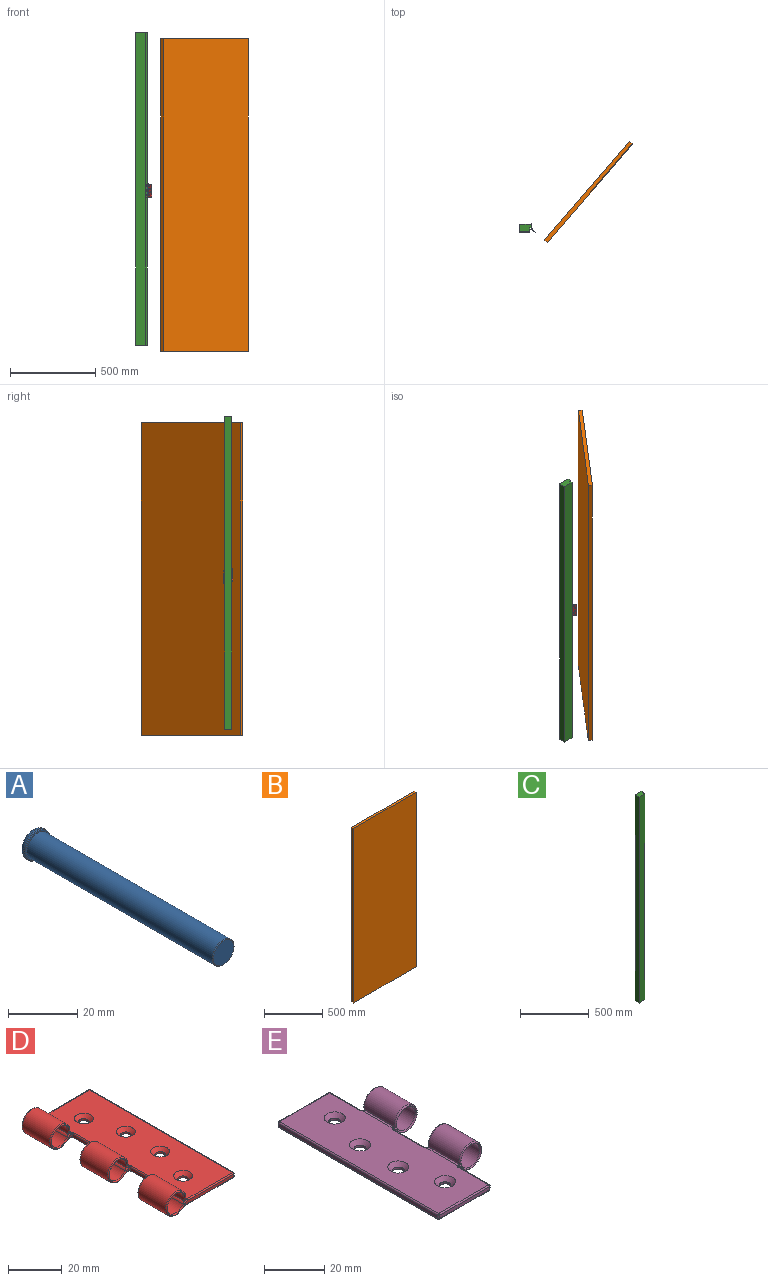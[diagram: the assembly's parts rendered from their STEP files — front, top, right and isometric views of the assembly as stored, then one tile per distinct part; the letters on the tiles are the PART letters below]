
ASSEMBLY  parts=5 mates=5
PART A: 8 faces, bbox 11x78.2x11 mm
  f0: cylinder r=4.4mm len=75.8mm, axis (0,1,0), area 2095.6mm2, adj f2,f5
  f1: plane 8.4x8.4mm, normal (0,-1,0), area 55.4mm2, adj f2
  f2: torus R=4.2mm, axis (0,-1,0), area 8.5mm2, adj f0,f1
  f3: cylinder r=5.1mm len=10.21mm, axis (0,-1,0), area 16mm2, adj f6,f7
  f4: plane 7.21x7.21mm, normal (0,1,0), area 40.8mm2, adj f6
  f5: plane 9.81x9.81mm, normal (0,-1,0), area 14.7mm2, adj f0,f7
  f6: torus R=3.6mm, axis (0,1,0), area 67.5mm2, adj f3,f4
  f7: torus R=4.9mm, axis (0,1,0), area 9.9mm2, adj f3,f5
PART B: 6 faces, bbox 762x23x1828.8 mm
  f0: plane 1828.8x23mm, normal (-1,0,0), area 42062.4mm2, adj f1,f3,f4,f5
  f1: plane 1828.8x762mm, normal (0,-1,0), area 1393545.6mm2, adj f0,f2,f4,f5
  f2: plane 1828.8x23mm, normal (1,0,0), area 42062.4mm2, adj f1,f3,f4,f5
  f3: plane 1828.8x762mm, normal (0,1,0), area 1393545.6mm2, adj f0,f2,f4,f5
  f4: plane 762x23mm, normal (0,0,1), area 17526mm2, adj f0,f1,f2,f3
  f5: plane 762x23mm, normal (0,0,-1), area 17526mm2, adj f0,f1,f2,f3
PART C: 8 faces, bbox 68.4x42x1828.8 mm
  f0: plane 1828.8x21mm, normal (1,0,0), area 38404.8mm2, adj f1,f5,f6,f7
  f1: plane 1828.8x8mm, normal (0,-1,0), area 14630.4mm2, adj f0,f2,f6,f7
  f2: plane 1828.8x21mm, normal (1,0,0), area 38404.8mm2, adj f1,f3,f6,f7
  f3: plane 1828.8x68.4mm, normal (0,1,0), area 125094mm2, adj f2,f4,f6,f7
  f4: plane 1828.8x42mm, normal (-1,0,0), area 76809.6mm2, adj f3,f5,f6,f7
  f5: plane 1828.8x60.4mm, normal (0,-1,0), area 110463.6mm2, adj f0,f4,f6,f7
  f6: plane 68.4x42mm, normal (0,0,1), area 2704.9mm2, adj f0,f1,f2,f3,f4,f5
  f7: plane 68.4x42mm, normal (0,0,-1), area 2704.9mm2, adj f0,f1,f2,f3,f4,f5
PART D: 94 faces, bbox 36.3x76x11.6 mm
  f0: cylinder r=5.25mm len=14.2mm, axis (0,1,0), area 412.4mm2, adj f2,f8,f69,f87
  f1: cylinder r=5.25mm len=14.2mm, axis (0,1,0), area 412.4mm2, adj f3,f9,f46,f78
  f2: plane 15.21x0.8mm, normal (0,0,-1), area 11.4mm2, adj f0,f4,f69,f71,f87,f90
  f3: plane 15.21x0.8mm, normal (0,0,-1), area 11.4mm2, adj f1,f5,f45,f46,f78,f80
  f4: cylinder r=4.5mm len=14.2mm, axis (0,1,0), area 382.9mm2, adj f2,f6,f71,f90
  f5: cylinder r=4.5mm len=14.2mm, axis (0,1,0), area 382.9mm2, adj f3,f7,f45,f80
  f6: cylinder r=2.39mm len=14.47mm, axis (0,1,0), area 36mm2, adj f4,f14,f73,f75,f92,f93
  f7: cylinder r=2.39mm len=14.33mm, axis (0,1,0), area 35.9mm2, adj f5,f14,f43,f82,f84
  f8: cylinder r=4.96mm len=14.47mm, axis (0,1,0), area 44.3mm2, adj f0,f16,f66,f68,f85,f88
  f9: cylinder r=4.96mm len=14.33mm, axis (0,1,0), area 44.3mm2, adj f1,f16,f48,f76,f77
  f10: cylinder r=5.25mm len=14.2mm, axis (0,1,0), area 412.4mm2, adj f11,f17,f51,f60
  f11: plane 15.21x0.8mm, normal (0,0,-1), area 11.4mm2, adj f10,f12,f51,f52,f60,f63
  f12: cylinder r=4.5mm len=14.2mm, axis (0,1,0), area 382.9mm2, adj f11,f13,f52,f63
  f13: cylinder r=2.39mm len=14.33mm, axis (0,1,0), area 35.9mm2, adj f12,f14,f49,f65,f67
  f14: plane 75x24mm, normal (0,0,1), area 1630.6mm2, adj f6,f7,f13,f21,f23,f25,f27,f41
  f15: plane 75x1.3mm, normal (1,0,0), area 97.5mm2, adj f38,f39,f42,f55
  f16: plane 75x24mm, normal (0,0,-1), area 1734.3mm2, adj f8,f9,f17,f20,f22,f24,f26,f50
  f17: cylinder r=4.96mm len=14.33mm, axis (0,1,0), area 44.3mm2, adj f10,f16,f54,f58,f61
  f18: plane 26.22x1.77mm, normal (0,-1,0), area 33.2mm2, adj f39,f47,f49,f52,f54,f56
  f19: plane 26.22x1.77mm, normal (0,1,0), area 33.2mm2, adj f38,f41,f43,f45,f48,f50
  f20: cylinder r=2mm len=4mm, axis (0,0,1), area 10.1mm2, adj f16,f21
  f21: cone r=2mm half-angle=45deg, axis (0,0,1), area 36.7mm2, adj f14,f20
  f22: cylinder r=2mm len=4mm, axis (0,0,1), area 10.1mm2, adj f16,f23
  f23: cone r=2mm half-angle=45deg, axis (0,0,1), area 36.7mm2, adj f14,f22
  f24: cylinder r=2mm len=4mm, axis (0,0,1), area 10.1mm2, adj f16,f25
  f25: cone r=2mm half-angle=45deg, axis (0,0,1), area 36.7mm2, adj f14,f24
  f26: cylinder r=2mm len=4mm, axis (0,0,1), area 10.1mm2, adj f16,f27
  f27: cone r=2mm half-angle=45deg, axis (0,0,1), area 36.7mm2, adj f14,f26
  f28: plane 14.2x1.3mm, normal (-1,0,0), area 18.5mm2, adj f34,f35,f81,f89
  f29: plane 1.72x1.7mm, normal (0,-1,0), area 1.3mm2, adj f34,f77,f80,f82
  f30: plane 1.72x1.7mm, normal (0,1,0), area 1.3mm2, adj f35,f88,f90,f92
  f31: plane 14.2x1.3mm, normal (-1,0,0), area 18.5mm2, adj f36,f37,f62,f72
  f32: plane 1.72x1.7mm, normal (0,1,0), area 1.3mm2, adj f36,f61,f63,f65
  f33: plane 1.72x1.7mm, normal (0,-1,0), area 1.3mm2, adj f37,f68,f71,f73
  f34: cylinder r=0.5mm len=1.32mm, axis (0,0,-1), area 1mm2, adj f28,f29,f76,f79,f84,f86
  f35: cylinder r=0.5mm len=1.32mm, axis (0,0,1), area 1mm2, adj f28,f30,f83,f85,f91,f93
  f36: cylinder r=0.5mm len=1.32mm, axis (0,0,-1), area 1mm2, adj f31,f32,f58,f59,f67,f70
  f37: cylinder r=0.5mm len=1.32mm, axis (0,0,1), area 1mm2, adj f31,f33,f64,f66,f74,f75
  f38: cylinder r=0.5mm len=1.3mm, axis (0,0,-1), area 1mm2, adj f15,f19,f40,f53
  f39: cylinder r=0.5mm len=1.3mm, axis (0,0,1), area 1mm2, adj f15,f18,f44,f57
  f40: sphere r=0.5mm, area 0.4mm2, adj f38,f41,f42
  f41: cylinder r=0.5mm len=24mm, axis (1,0,0), area 18.8mm2, adj f14,f19,f40,f43
  f42: cylinder r=0.5mm len=75mm, axis (0,1,0), area 58.9mm2, adj f14,f15,f40,f44
  f43: torus R=1.89mm, axis (0,-1,0), area 1.8mm2, adj f7,f19,f41,f45
  f44: sphere r=0.5mm, area 0.4mm2, adj f39,f42,f47
  f45: torus R=5mm, axis (0,-1,0), area 18.5mm2, adj f3,f5,f19,f43,f46,f48
  f46: torus R=4.75mm, axis (0,-1,0), area 18.7mm2, adj f1,f3,f45,f48
  f47: cylinder r=0.5mm len=24mm, axis (-1,0,0), area 18.8mm2, adj f14,f18,f44,f49
  f48: torus R=5.46mm, axis (0,-1,0), area 2.5mm2, adj f9,f19,f45,f46,f50
  f49: torus R=1.89mm, axis (0,-1,0), area 1.8mm2, adj f13,f18,f47,f52
  f50: cylinder r=0.5mm len=24mm, axis (-1,0,0), area 18.8mm2, adj f16,f19,f48,f53
  f51: torus R=4.75mm, axis (0,-1,0), area 18.7mm2, adj f10,f11,f52,f54
  f52: torus R=5mm, axis (0,-1,0), area 18.5mm2, adj f11,f12,f18,f49,f51,f54
  f53: sphere r=0.5mm, area 0.4mm2, adj f38,f50,f55
  f54: torus R=5.46mm, axis (0,-1,0), area 2.5mm2, adj f17,f18,f51,f52,f56
  f55: cylinder r=0.5mm len=75mm, axis (0,1,0), area 58.9mm2, adj f15,f16,f53,f57
  f56: cylinder r=0.5mm len=24mm, axis (1,0,0), area 18.8mm2, adj f16,f18,f54,f57
  f57: sphere r=0.5mm, area 0.4mm2, adj f39,f55,f56
  f58: bspline ~0.72x0.61mm, area 0.3mm2, adj f17,f36,f59,f61
  f59: torus R=1mm, axis (0,0,1), area 0.6mm2, adj f16,f36,f58,f62
  f60: torus R=4.75mm, axis (0,-1,0), area 18.7mm2, adj f10,f11,f61,f63
  f61: torus R=5.46mm, axis (0,-1,0), area 2.1mm2, adj f17,f32,f58,f60,f63
  f62: cylinder r=0.5mm len=14.2mm, axis (0,-1,0), area 11.2mm2, adj f16,f31,f59,f64
  f63: torus R=5mm, axis (0,-1,0), area 18.5mm2, adj f11,f12,f32,f60,f61,f65
  f64: torus R=1mm, axis (0,0,1), area 0.6mm2, adj f16,f37,f62,f66
  f65: torus R=1.89mm, axis (0,-1,0), area 1.4mm2, adj f13,f32,f63,f67
  f66: bspline ~0.72x0.61mm, area 0.3mm2, adj f8,f37,f64,f68
  f67: bspline ~0.83x0.6mm, area 0.3mm2, adj f13,f36,f65,f70
  f68: torus R=5.46mm, axis (0,-1,0), area 2.1mm2, adj f8,f33,f66,f69,f71
  f69: torus R=4.75mm, axis (0,-1,0), area 18.7mm2, adj f0,f2,f68,f71
  f70: torus R=1mm, axis (0,0,-1), area 0.6mm2, adj f14,f36,f67,f72
  f71: torus R=5mm, axis (0,-1,0), area 18.5mm2, adj f2,f4,f33,f68,f69,f73
  f72: cylinder r=0.5mm len=14.2mm, axis (0,-1,0), area 11.2mm2, adj f14,f31,f70,f74
  f73: torus R=1.89mm, axis (0,-1,0), area 1.4mm2, adj f6,f33,f71,f75
  f74: torus R=1mm, axis (0,0,-1), area 0.6mm2, adj f14,f37,f72,f75
  f75: bspline ~0.83x0.6mm, area 0.3mm2, adj f6,f37,f73,f74
  f76: bspline ~0.72x0.61mm, area 0.3mm2, adj f9,f34,f77,f79
  f77: torus R=5.46mm, axis (0,-1,0), area 2.1mm2, adj f9,f29,f76,f78,f80
  f78: torus R=4.75mm, axis (0,-1,0), area 18.7mm2, adj f1,f3,f77,f80
  f79: torus R=1mm, axis (0,0,1), area 0.6mm2, adj f16,f34,f76,f81
  f80: torus R=5mm, axis (0,-1,0), area 18.5mm2, adj f3,f5,f29,f77,f78,f82
  f81: cylinder r=0.5mm len=14.2mm, axis (0,1,0), area 11.2mm2, adj f16,f28,f79,f83
  f82: torus R=1.89mm, axis (0,-1,0), area 1.4mm2, adj f7,f29,f80,f84
  f83: torus R=1mm, axis (0,0,1), area 0.6mm2, adj f16,f35,f81,f85
  f84: bspline ~0.83x0.6mm, area 0.3mm2, adj f7,f34,f82,f86
  f85: bspline ~0.72x0.61mm, area 0.3mm2, adj f8,f35,f83,f88
  f86: torus R=1mm, axis (0,0,-1), area 0.6mm2, adj f14,f34,f84,f89
  f87: torus R=4.75mm, axis (0,-1,0), area 18.7mm2, adj f0,f2,f88,f90
  f88: torus R=5.46mm, axis (0,-1,0), area 2.1mm2, adj f8,f30,f85,f87,f90
  f89: cylinder r=0.5mm len=14.2mm, axis (0,-1,0), area 11.2mm2, adj f14,f28,f86,f91
  f90: torus R=5mm, axis (0,-1,0), area 18.5mm2, adj f2,f4,f30,f87,f88,f92
  f91: torus R=1mm, axis (0,0,-1), area 0.6mm2, adj f14,f35,f89,f93
  f92: torus R=1.89mm, axis (0,-1,0), area 1.4mm2, adj f6,f30,f90,f93
  f93: bspline ~0.83x0.6mm, area 0.3mm2, adj f6,f35,f91,f92
PART E: 90 faces, bbox 36.3x76x11.6 mm
  f0: cylinder r=5.25mm len=14.2mm, axis (0,1,0), area 412.4mm2, adj f2,f8,f59,f83
  f1: cylinder r=5.25mm len=14.2mm, axis (0,1,0), area 412.4mm2, adj f3,f9,f46,f74
  f2: plane 15.21x0.8mm, normal (0,0,-1), area 11.4mm2, adj f0,f4,f59,f61,f83,f86
  f3: plane 15.21x0.8mm, normal (0,0,-1), area 11.4mm2, adj f1,f5,f46,f49,f74,f76
  f4: cylinder r=4.5mm len=14.2mm, axis (0,1,0), area 382.9mm2, adj f2,f6,f61,f86
  f5: cylinder r=4.5mm len=14.2mm, axis (0,1,0), area 382.9mm2, adj f3,f7,f49,f76
  f6: cylinder r=2.39mm len=14.47mm, axis (0,1,0), area 36mm2, adj f4,f10,f63,f65,f88,f89
  f7: cylinder r=2.39mm len=14.47mm, axis (0,1,0), area 36mm2, adj f5,f10,f51,f53,f78,f80
  f8: cylinder r=4.96mm len=14.47mm, axis (0,1,0), area 44.3mm2, adj f0,f12,f56,f58,f81,f84
  f9: cylinder r=4.96mm len=14.47mm, axis (0,1,0), area 44.3mm2, adj f1,f12,f44,f47,f72,f73
  f10: plane 75x24mm, normal (0,0,1), area 1623.5mm2, adj f6,f7,f16,f18,f20,f22,f55,f57
  f11: plane 75x1.3mm, normal (-1,0,0), area 97.5mm2, adj f36,f37,f43,f66
  f12: plane 75x24mm, normal (0,0,-1), area 1727.2mm2, adj f8,f9,f15,f17,f19,f21,f39,f40
  f13: plane 23.5x1.3mm, normal (0,-1,0), area 30.6mm2, adj f30,f37,f39,f62
  f14: plane 23.5x1.3mm, normal (0,1,0), area 30.6mm2, adj f34,f36,f48,f70
  f15: cylinder r=2mm len=4mm, axis (0,0,1), area 10.1mm2, adj f12,f16
  f16: cone r=2mm half-angle=45deg, axis (0,0,1), area 36.7mm2, adj f10,f15
  f17: cylinder r=2mm len=4mm, axis (0,0,1), area 10.1mm2, adj f12,f18
  f18: cone r=2mm half-angle=45deg, axis (0,0,1), area 36.7mm2, adj f10,f17
  f19: cylinder r=2mm len=4mm, axis (0,0,1), area 10.1mm2, adj f12,f20
  f20: cone r=2mm half-angle=45deg, axis (0,0,1), area 36.7mm2, adj f10,f19
  f21: cylinder r=2mm len=4mm, axis (0,0,1), area 10.1mm2, adj f12,f22
  f22: cone r=2mm half-angle=45deg, axis (0,0,1), area 36.7mm2, adj f10,f21
  f23: plane 14.2x1.3mm, normal (1,0,0), area 18.5mm2, adj f30,f31,f40,f57
  f24: plane 1.72x1.7mm, normal (0,-1,0), area 1.3mm2, adj f31,f47,f49,f51
  f25: plane 14.2x1.3mm, normal (1,0,0), area 18.5mm2, adj f32,f33,f77,f85
  f26: plane 1.72x1.7mm, normal (0,1,0), area 1.3mm2, adj f32,f73,f76,f78
  f27: plane 1.72x1.7mm, normal (0,-1,0), area 1.3mm2, adj f33,f84,f86,f88
  f28: plane 14.2x1.3mm, normal (1,0,0), area 18.5mm2, adj f34,f35,f52,f69
  f29: plane 1.72x1.7mm, normal (0,1,0), area 1.3mm2, adj f35,f58,f61,f63
  f30: cylinder r=0.5mm len=1.3mm, axis (0,0,1), area 1mm2, adj f13,f23,f38,f60
  f31: cylinder r=0.5mm len=1.32mm, axis (0,0,1), area 1mm2, adj f23,f24,f42,f44,f53,f55
  f32: cylinder r=0.5mm len=1.32mm, axis (0,0,-1), area 1mm2, adj f25,f26,f72,f75,f80,f82
  f33: cylinder r=0.5mm len=1.32mm, axis (0,0,1), area 1mm2, adj f25,f27,f79,f81,f87,f89
  f34: cylinder r=0.5mm len=1.3mm, axis (0,0,-1), area 1mm2, adj f14,f28,f50,f71
  f35: cylinder r=0.5mm len=1.32mm, axis (0,0,-1), area 1mm2, adj f28,f29,f54,f56,f65,f67
  f36: cylinder r=0.5mm len=1.3mm, axis (0,0,-1), area 1mm2, adj f11,f14,f45,f68
  f37: cylinder r=0.5mm len=1.3mm, axis (0,0,1), area 1mm2, adj f11,f13,f41,f64
  f38: sphere r=0.5mm, area 0.4mm2, adj f30,f39,f40
  f39: cylinder r=0.5mm len=23.5mm, axis (-1,0,0), area 18.5mm2, adj f12,f13,f38,f41
  f40: cylinder r=0.5mm len=14.2mm, axis (0,1,0), area 11.2mm2, adj f12,f23,f38,f42
  f41: sphere r=0.5mm, area 0.4mm2, adj f37,f39,f43
  f42: torus R=1mm, axis (0,0,1), area 0.6mm2, adj f12,f31,f40,f44
  f43: cylinder r=0.5mm len=75mm, axis (0,1,0), area 58.9mm2, adj f11,f12,f41,f45
  f44: bspline ~0.72x0.61mm, area 0.3mm2, adj f9,f31,f42,f47
  f45: sphere r=0.5mm, area 0.4mm2, adj f36,f43,f48
  f46: torus R=4.75mm, axis (0,1,0), area 18.7mm2, adj f1,f3,f47,f49
  f47: torus R=5.46mm, axis (0,1,0), area 2.1mm2, adj f9,f24,f44,f46,f49
  f48: cylinder r=0.5mm len=23.5mm, axis (1,0,0), area 18.5mm2, adj f12,f14,f45,f50
  f49: torus R=5mm, axis (0,1,0), area 18.5mm2, adj f3,f5,f24,f46,f47,f51
  f50: sphere r=0.5mm, area 0.4mm2, adj f34,f48,f52
  f51: torus R=1.89mm, axis (0,1,0), area 1.4mm2, adj f7,f24,f49,f53
  f52: cylinder r=0.5mm len=14.2mm, axis (0,-1,0), area 11.2mm2, adj f12,f28,f50,f54
  f53: bspline ~0.83x0.6mm, area 0.3mm2, adj f7,f31,f51,f55
  f54: torus R=1mm, axis (0,0,1), area 0.6mm2, adj f12,f35,f52,f56
  f55: torus R=1mm, axis (0,0,-1), area 0.6mm2, adj f10,f31,f53,f57
  f56: bspline ~0.72x0.61mm, area 0.3mm2, adj f8,f35,f54,f58
  f57: cylinder r=0.5mm len=14.2mm, axis (0,1,0), area 11.2mm2, adj f10,f23,f55,f60
  f58: torus R=5.46mm, axis (0,1,0), area 2.1mm2, adj f8,f29,f56,f59,f61
  f59: torus R=4.75mm, axis (0,1,0), area 18.7mm2, adj f0,f2,f58,f61
  f60: sphere r=0.5mm, area 0.4mm2, adj f30,f57,f62
  f61: torus R=5mm, axis (0,1,0), area 18.5mm2, adj f2,f4,f29,f58,f59,f63
  f62: cylinder r=0.5mm len=23.5mm, axis (1,0,0), area 18.5mm2, adj f10,f13,f60,f64
  f63: torus R=1.89mm, axis (0,1,0), area 1.4mm2, adj f6,f29,f61,f65
  f64: sphere r=0.5mm, area 0.4mm2, adj f37,f62,f66
  f65: bspline ~0.83x0.6mm, area 0.3mm2, adj f6,f35,f63,f67
  f66: cylinder r=0.5mm len=75mm, axis (0,1,0), area 58.9mm2, adj f10,f11,f64,f68
  f67: torus R=1mm, axis (0,0,-1), area 0.6mm2, adj f10,f35,f65,f69
  f68: sphere r=0.5mm, area 0.4mm2, adj f36,f66,f70
  f69: cylinder r=0.5mm len=14.2mm, axis (0,1,0), area 11.2mm2, adj f10,f28,f67,f71
  f70: cylinder r=0.5mm len=23.5mm, axis (-1,0,0), area 18.5mm2, adj f10,f14,f68,f71
  f71: sphere r=0.5mm, area 0.4mm2, adj f34,f69,f70
  f72: bspline ~0.72x0.61mm, area 0.3mm2, adj f9,f32,f73,f75
  f73: torus R=5.46mm, axis (0,1,0), area 2.1mm2, adj f9,f26,f72,f74,f76
  f74: torus R=4.75mm, axis (0,1,0), area 18.7mm2, adj f1,f3,f73,f76
  f75: torus R=1mm, axis (0,0,1), area 0.6mm2, adj f12,f32,f72,f77
  f76: torus R=5mm, axis (0,1,0), area 18.5mm2, adj f3,f5,f26,f73,f74,f78
  f77: cylinder r=0.5mm len=14.2mm, axis (0,1,0), area 11.2mm2, adj f12,f25,f75,f79
  f78: torus R=1.89mm, axis (0,1,0), area 1.4mm2, adj f7,f26,f76,f80
  f79: torus R=1mm, axis (0,0,1), area 0.6mm2, adj f12,f33,f77,f81
  f80: bspline ~0.83x0.6mm, area 0.3mm2, adj f7,f32,f78,f82
  f81: bspline ~0.72x0.61mm, area 0.3mm2, adj f8,f33,f79,f84
  f82: torus R=1mm, axis (0,0,-1), area 0.6mm2, adj f10,f32,f80,f85
  f83: torus R=4.75mm, axis (0,1,0), area 18.7mm2, adj f0,f2,f84,f86
  f84: torus R=5.46mm, axis (0,1,0), area 2.1mm2, adj f8,f27,f81,f83,f86
  f85: cylinder r=0.5mm len=14.2mm, axis (0,1,0), area 11.2mm2, adj f10,f25,f82,f87
  f86: torus R=5mm, axis (0,1,0), area 18.5mm2, adj f2,f4,f27,f83,f84,f88
  f87: torus R=1mm, axis (0,0,-1), area 0.6mm2, adj f10,f33,f85,f89
  f88: torus R=1.89mm, axis (0,1,0), area 1.4mm2, adj f6,f27,f86,f89
  f89: bspline ~0.83x0.6mm, area 0.3mm2, adj f6,f33,f87,f88
PLACE A rot(axis=(-0.58,0.58,-0.58),120deg) t=(-29.11,39.24,6.55)mm
PLACE B rot(axis=(-0.91,-0.42,0),180deg) t=(59.18,-30.23,930.25)mm
PLACE C t=(-21.79,44.9,-861.75)mm fixed
PLACE D rot(axis=(-0.89,0.33,-0.33),96.9deg) t=(-33.32,36.38,3.85)mm
PLACE E rot(axis=(-0.58,0.58,-0.58),120deg) t=(-29.11,39.24,-11.35)mm
MATE revolute D.f0 <-> A.f0  axis (0,0,-1) through (-28.11,33.24,4.35)mm
MATE fastened C.f2 <-> E.f21  axis (1,0,0) through (-31.41,48.74,52.65)mm
MATE planar D.f14 <-> B.f0  axis (0.65,0.76,0) through (-15.01,20.69,41.85)mm
MATE revolute E.f0 <-> D.f0  axis (0,0,-1) through (-28.11,33.24,34.75)mm
MATE planar E.f12 <-> C.f2  axis (-1,0,0) through (-31.41,51.39,26.65)mm
